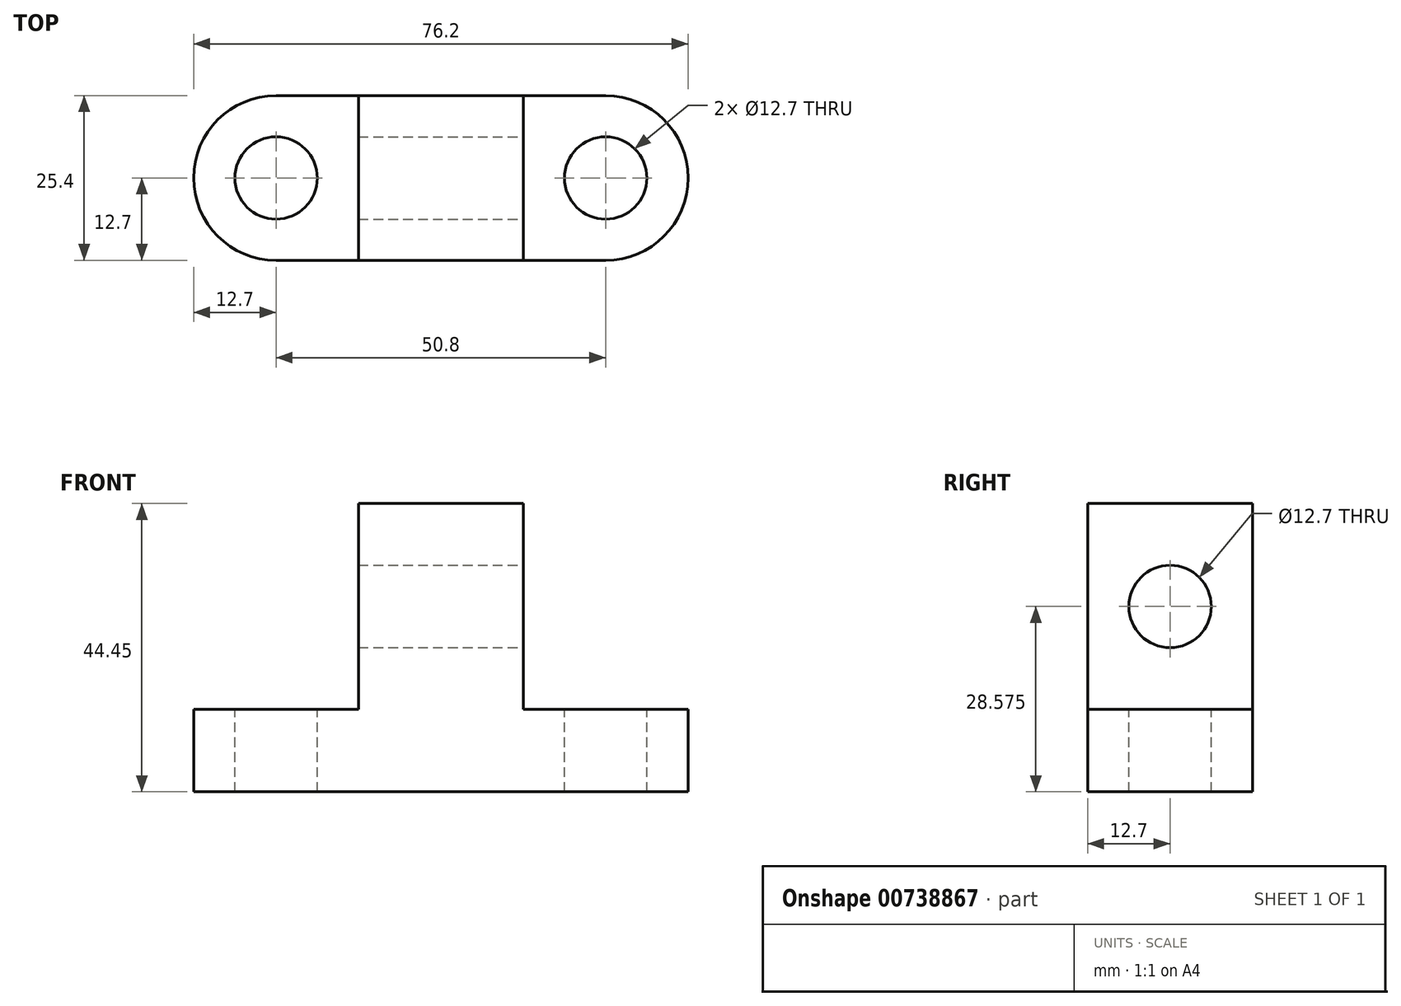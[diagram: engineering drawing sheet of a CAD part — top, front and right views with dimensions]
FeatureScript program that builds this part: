
annotation { "Feature Type Name" : "Feature", "Feature Type Description" : "" }
export const myFeature = defineFeature(function(context is Context, id is Id, definition is map)
    precondition{}
    {
        {
            var Q0;
            Q0=qCreatedBy(makeId("Front.planeOp"),FACE);
            var sketch = newSketch(context, id + "F0", { "sketchPlane" : qUnion([Q0])});
            skLineSegment(sketch, "E0", {"start": v(0, 0) * mm, "end": v(76.2, 0) * mm});
            skLineSegment(sketch, "E1", {"start": v(76.2, 0) * mm, "end": v(76.2, 44.45) * mm});
            skLineSegment(sketch, "E2", {"start": v(76.2, 44.45) * mm, "end": v(0, 44.45) * mm});
            skLineSegment(sketch, "E3", {"start": v(0, 44.45) * mm, "end": v(0, 0) * mm});
            skSolve(sketch);
        }
        {
            var Q0;
            Q0 = qSketchRegion(id + "F0", true);
            var Q1;
            Q1=makeQuery(id+"F0.imprint","IMPRINT",FACE,{"disambiguationData":[TD([[makeQuery(id+"F0.imprint","IMPRINT",EDGE,{"derivedFrom":sQuery(id+"F0.wireOp",EDGE,"E0")}),1.0]])]});
            extrude(context, id + "F1", {"entities" : qUnion([Q0, Q1]), "depth" : 25.4 * mm, "offsetDistance" : 25.4 * mm});
        }
        {
            var Q0;
            Q0=makeQuery(id+"F1.opExtrude","CAP_FACE",FACE,{"disambiguationData":[OSD([sQuery(id+"F0.wireOp",EDGE,"E0"),sQuery(id+"F0.wireOp",EDGE,"E1"),sQuery(id+"F0.wireOp",EDGE,"E2"),sQuery(id+"F0.wireOp",EDGE,"E3")])],"isStart":false});
            var sketch = newSketch(context, id + "F2", { "sketchPlane" : qUnion([Q0])});
            skLineSegment(sketch, "E4", {"start": v(25.4, 44.45) * mm, "end": v(25.4, 12.7) * mm});
            skLineSegment(sketch, "E5", {"start": v(25.4, 12.7) * mm, "end": v(0, 12.7) * mm});
            skLineSegment(sketch, "E6", {"start": v(50.8, 44.45) * mm, "end": v(50.8, 12.7) * mm});
            skLineSegment(sketch, "E7", {"start": v(50.8, 12.7) * mm, "end": v(76.2, 12.7) * mm});
            skSolve(sketch);
        }
        {
            var Q0;
            Q0 = qSketchRegion(id + "F2", true);
            var Q1;
            {var subQ0=sQuery(id+"F2.wireOp",EDGE,"E4");Q1=makeQuery(id+"F2.imprint","IMPRINT",FACE,{"disambiguationData":[TD([[makeQuery(id+"F2.imprint","IMPRINT",EDGE,{"derivedFrom":subQ0}),-1.0]])]});}
            var Q2;
            {var subQ0=sQuery(id+"F2.wireOp",EDGE,"E6");Q2=makeQuery(id+"F2.imprint","IMPRINT",FACE,{"disambiguationData":[TD([[makeQuery(id+"F2.imprint","IMPRINT",EDGE,{"derivedFrom":subQ0}),1.0]])]});}
            extrude(context, id + "F3", {"entities" : qUnion([Q0, Q1, Q2]), "operationType" : NewBodyOperationType.REMOVE, "oppositeDirection" : true, "depth" : 25.4 * mm, "offsetDistance" : 25.4 * mm});
        }
        {
            var Q0;
            Q0=makeQuery(id+"F3.boolean.opBoolean","COPY",FACE,{"derivedFrom":makeQuery(id+"F3.opExtrude","SWEPT_FACE",FACE,{"disambiguationData":[OSD([sQuery(id+"F2.wireOp",EDGE,"E6")])]})});
            var sketch = newSketch(context, id + "F4", { "sketchPlane" : qUnion([Q0])});
            skCircle(sketch, "E8", {"center": v(-12.7, 28.58) * mm, "radius": 6.35 * mm});
            skArc(sketch, "E9", {"start": v(0, 28.58) * mm, "mid": v(-12.7, 44.45) * mm, "end": v(-25.4, 28.58) * mm});
            skSolve(sketch);
        }
        {
            var Q0;
            Q0 = qSketchRegion(id + "F4", true);
            var Q1;
            {var subQ0=sQuery(id+"F4.wireOp",EDGE,"E9");var subQ1=sQuery(id+"F2.wireOp",EDGE,"E6");var subQ2=makeQuery(id+"F3.boolean.opBoolean","COPY",EDGE,{"derivedFrom":makeQuery(id+"F3.opExtrude","CAP_EDGE",EDGE,{"disambiguationData":[OSD([subQ1])],"isStart":false})});var subQ3=makeQuery(id+"F4.imprint","INTERSECT",VERTEX,{"disambiguationData":[OD(1.0)],"derivedFrom":[subQ2,subQ0]});Q1=makeQuery(id+"F4.imprint","IMPRINT",FACE,{"disambiguationData":[TD([[makeQuery(id+"F4.imprint","IMPRINT",EDGE,{"disambiguationData":[TD([[subQ3,-1.0]])],"derivedFrom":subQ0}),-1.0]])]});}
            var Q2;
            {var subQ0=sQuery(id+"F4.wireOp",EDGE,"E9");var subQ1=sQuery(id+"F2.wireOp",EDGE,"E6");var subQ4=makeQuery(id+"F3.boolean.opBoolean","COPY",EDGE,{"derivedFrom":makeQuery(id+"F3.opExtrude","CAP_EDGE",EDGE,{"disambiguationData":[OSD([subQ1])],"isStart":true})});var subQ5=makeQuery(id+"F4.imprint","INTERSECT",VERTEX,{"disambiguationData":[OD(1.0)],"derivedFrom":[subQ4,subQ0]});Q2=makeQuery(id+"F4.imprint","IMPRINT",FACE,{"disambiguationData":[TD([[makeQuery(id+"F4.imprint","IMPRINT",EDGE,{"disambiguationData":[TD([[subQ5,1.0]])],"derivedFrom":subQ0}),-1.0]])]});}
            extrude(context, id + "F5", {"entities" : qUnion([Q0, Q1, Q2]), "operationType" : NewBodyOperationType.REMOVE, "oppositeDirection" : true, "depth" : 25.4 * mm, "offsetDistance" : 25.4 * mm});
        }
        {
            var Q0;
            Q0=makeQuery(id+"F3.boolean.opBoolean","COPY",FACE,{"derivedFrom":makeQuery(id+"F3.opExtrude","SWEPT_FACE",FACE,{"disambiguationData":[OSD([sQuery(id+"F2.wireOp",EDGE,"E7")])]})});
            var sketch = newSketch(context, id + "F6", { "sketchPlane" : qUnion([Q0])});
            skCircle(sketch, "E10", {"center": v(63.5, -12.7) * mm, "radius": 6.35 * mm});
            skArc(sketch, "E11", {"start": v(63.5, -25.4) * mm, "mid": v(76.2, -12.7) * mm, "end": v(63.5, 0) * mm});
            skSolve(sketch);
        }
        {
            var Q0;
            Q0 = qSketchRegion(id + "F6", true);
            var Q1;
            {var subQ0=sQuery(id+"F6.wireOp",EDGE,"E11");var subQ1=sQuery(id+"F2.wireOp",EDGE,"E7");var subQ2=makeQuery(id+"F3.boolean.opBoolean","COPY",EDGE,{"derivedFrom":makeQuery(id+"F3.opExtrude","CAP_EDGE",EDGE,{"disambiguationData":[OSD([subQ1])],"isStart":false})});var subQ3=makeQuery(id+"F6.imprint","INTERSECT",VERTEX,{"derivedFrom":[subQ2,subQ0]});Q1=makeQuery(id+"F6.imprint","IMPRINT",FACE,{"disambiguationData":[TD([[makeQuery(id+"F6.imprint","IMPRINT",EDGE,{"disambiguationData":[TD([[subQ3,1.0]])],"derivedFrom":subQ0}),-1.0]])]});}
            var Q2;
            {var subQ0=sQuery(id+"F6.wireOp",EDGE,"E11");var subQ1=sQuery(id+"F2.wireOp",EDGE,"E7");var subQ2=makeQuery(id+"F3.boolean.opBoolean","COPY",EDGE,{"derivedFrom":makeQuery(id+"F3.opExtrude","CAP_EDGE",EDGE,{"disambiguationData":[OSD([subQ1])],"isStart":true})});var subQ3=makeQuery(id+"F6.imprint","INTERSECT",VERTEX,{"derivedFrom":[subQ2,subQ0]});Q2=makeQuery(id+"F6.imprint","IMPRINT",FACE,{"disambiguationData":[TD([[makeQuery(id+"F6.imprint","IMPRINT",EDGE,{"disambiguationData":[TD([[subQ3,-1.0]])],"derivedFrom":subQ0}),-1.0]])]});}
            extrude(context, id + "F7", {"entities" : qUnion([Q0, Q1, Q2]), "operationType" : NewBodyOperationType.REMOVE, "oppositeDirection" : true, "depth" : 25.4 * mm, "offsetDistance" : 25.4 * mm});
        }
        {
            var Q0;
            Q0=makeQuery(id+"F3.boolean.opBoolean","COPY",FACE,{"derivedFrom":makeQuery(id+"F3.opExtrude","SWEPT_FACE",FACE,{"disambiguationData":[OSD([sQuery(id+"F2.wireOp",EDGE,"E5")])]})});
            var sketch = newSketch(context, id + "F8", { "sketchPlane" : qUnion([Q0])});
            skCircle(sketch, "E12", {"center": v(12.7, -12.7) * mm, "radius": 6.35 * mm});
            skArc(sketch, "E13", {"start": v(12.7, 0) * mm, "mid": v(0, -12.7) * mm, "end": v(12.7, -25.4) * mm});
            skSolve(sketch);
        }
        {
            var Q0;
            {var subQ0=sQuery(id+"F8.wireOp",EDGE,"E13");var subQ1=sQuery(id+"F2.wireOp",EDGE,"E5");var subQ2=makeQuery(id+"F3.boolean.opBoolean","COPY",EDGE,{"derivedFrom":makeQuery(id+"F3.opExtrude","CAP_EDGE",EDGE,{"disambiguationData":[OSD([subQ1])],"isStart":false})});var subQ3=makeQuery(id+"F8.imprint","INTERSECT",VERTEX,{"derivedFrom":[subQ2,subQ0]});Q0=makeQuery(id+"F8.imprint","IMPRINT",FACE,{"disambiguationData":[TD([[makeQuery(id+"F8.imprint","IMPRINT",EDGE,{"disambiguationData":[TD([[subQ3,-1.0]])],"derivedFrom":subQ0}),-1.0]])]});}
            var Q1;
            Q1=makeQuery(id+"F8.imprint","IMPRINT",FACE,{"disambiguationData":[TD([[makeQuery(id+"F8.imprint","IMPRINT",EDGE,{"derivedFrom":sQuery(id+"F8.wireOp",EDGE,"E12")}),1.0]])]});
            var Q2;
            {var subQ0=sQuery(id+"F8.wireOp",EDGE,"E13");var subQ1=sQuery(id+"F2.wireOp",EDGE,"E5");var subQ2=makeQuery(id+"F3.boolean.opBoolean","COPY",EDGE,{"derivedFrom":makeQuery(id+"F3.opExtrude","CAP_EDGE",EDGE,{"disambiguationData":[OSD([subQ1])],"isStart":true})});var subQ3=makeQuery(id+"F8.imprint","INTERSECT",VERTEX,{"derivedFrom":[subQ2,subQ0]});Q2=makeQuery(id+"F8.imprint","IMPRINT",FACE,{"disambiguationData":[TD([[makeQuery(id+"F8.imprint","IMPRINT",EDGE,{"disambiguationData":[TD([[subQ3,1.0]])],"derivedFrom":subQ0}),-1.0]])]});}
            extrude(context, id + "F9", {"entities" : qUnion([Q0, Q1, Q2]), "operationType" : NewBodyOperationType.REMOVE, "oppositeDirection" : true, "depth" : 25.4 * mm, "offsetDistance" : 25.4 * mm});
        }
    });
